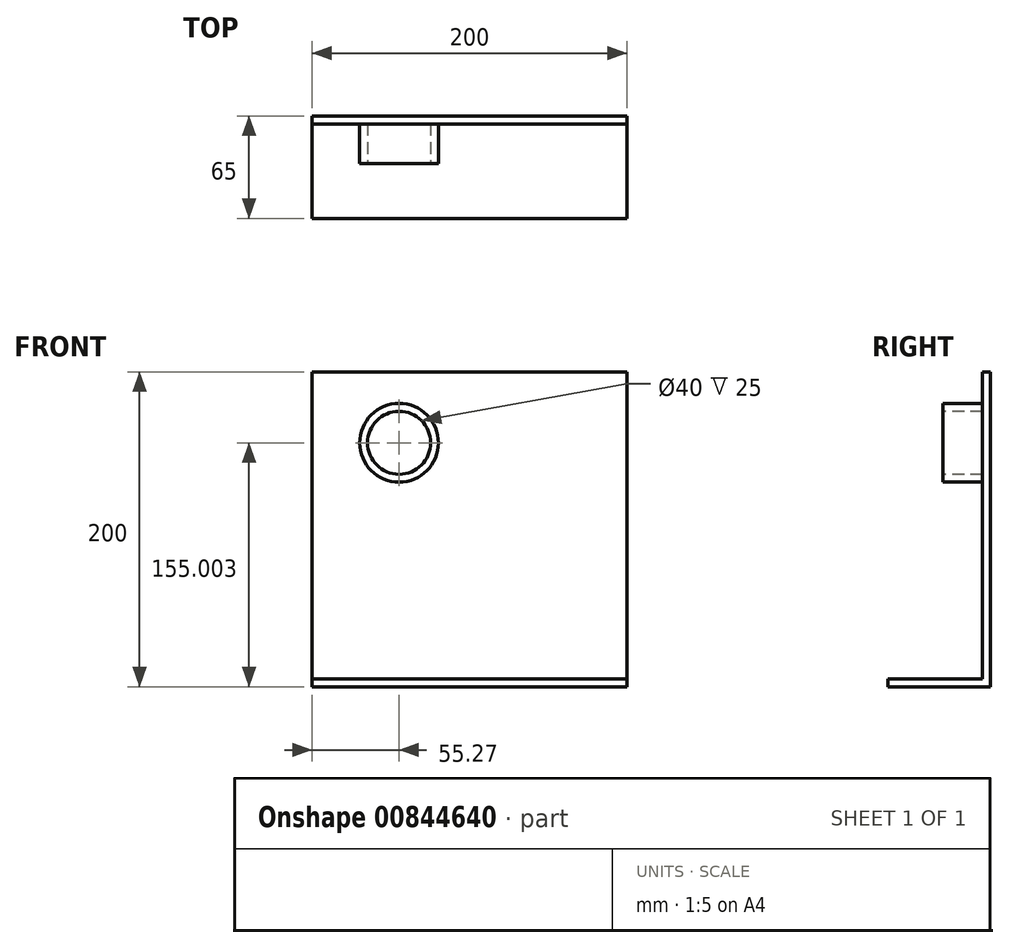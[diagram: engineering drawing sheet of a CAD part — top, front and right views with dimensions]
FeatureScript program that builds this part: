
annotation { "Feature Type Name" : "Feature", "Feature Type Description" : "" }
export const myFeature = defineFeature(function(context is Context, id is Id, definition is map)
    precondition{}
    {
        {
            var Q0;
            Q0=qCreatedBy(makeId("Front.planeOp"),FACE);
            var sketch = newSketch(context, id + "F0", { "sketchPlane" : qUnion([Q0])});
            skLineSegment(sketch, "E0.bottom", {"start": v(-55.27, -42.78) * mm, "end": v(144.73, -42.78) * mm});
            skLineSegment(sketch, "E0.top", {"start": v(-55.27, 157.22) * mm, "end": v(144.73, 157.22) * mm});
            skLineSegment(sketch, "E0.left", {"start": v(-55.27, -42.78) * mm, "end": v(-55.27, 157.22) * mm});
            skLineSegment(sketch, "E0.right", {"start": v(144.73, -42.78) * mm, "end": v(144.73, 157.22) * mm});
            skSolve(sketch);
        }
        {
            var Q0;
            Q0 = qSketchRegion(id + "F0", true);
            extrude(context, id + "F1", {"entities" : qUnion([Q0]), "depth" : 5 * mm, "offsetDistance" : 25 * mm});
        }
        {
            var Q0;
            Q0=makeQuery(id+"F1.opExtrude","CAP_FACE",FACE,{"disambiguationData":[OSD([sQuery(id+"F0.wireOp",EDGE,"E0.bottom"),sQuery(id+"F0.wireOp",EDGE,"E0.top"),sQuery(id+"F0.wireOp",EDGE,"E0.left"),sQuery(id+"F0.wireOp",EDGE,"E0.right")])],"isStart":false});
            var sketch = newSketch(context, id + "F2", { "sketchPlane" : qUnion([Q0])});
            skLineSegment(sketch, "E1.bottom", {"start": v(-55.27, -42.78) * mm, "end": v(144.73, -42.78) * mm});
            skLineSegment(sketch, "E1.top", {"start": v(-55.27, -37.78) * mm, "end": v(144.73, -37.78) * mm});
            skLineSegment(sketch, "E1.left", {"start": v(-55.27, -42.78) * mm, "end": v(-55.27, -37.78) * mm});
            skLineSegment(sketch, "E1.right", {"start": v(144.73, -42.78) * mm, "end": v(144.73, -37.78) * mm});
            skSolve(sketch);
        }
        {
            var Q0;
            Q0=makeQuery(id+"F2.imprint","IMPRINT",FACE,{"disambiguationData":[TD([[makeQuery(id+"F2.imprint","IMPRINT",EDGE,{"derivedFrom":sQuery(id+"F2.wireOp",EDGE,"E1.bottom")}),1.0]])]});
            extrude(context, id + "F3", {"entities" : qUnion([Q0]), "operationType" : NewBodyOperationType.ADD, "depth" : 60 * mm, "offsetDistance" : 25 * mm});
        }
        {
            var Q0;
            Q0=makeQuery(id+"F1.opExtrude","CAP_FACE",FACE,{"disambiguationData":[OSD([sQuery(id+"F0.wireOp",EDGE,"E0.bottom"),sQuery(id+"F0.wireOp",EDGE,"E0.top"),sQuery(id+"F0.wireOp",EDGE,"E0.left"),sQuery(id+"F0.wireOp",EDGE,"E0.right")])],"isStart":false});
            var sketch = newSketch(context, id + "F4", { "sketchPlane" : qUnion([Q0])});
            skCircle(sketch, "E2", {"center": v(0, 112.22) * mm, "radius": 25 * mm});
            skSolve(sketch);
        }
        {
            var Q0;
            Q0 = qSketchRegion(id + "F4", true);
            extrude(context, id + "F5", {"entities" : qUnion([Q0]), "operationType" : NewBodyOperationType.ADD, "depth" : 25 * mm, "offsetDistance" : 25 * mm});
        }
        {
            var Q0;
            Q0=makeQuery(id+"F5.opExtrude","CAP_FACE",FACE,{"disambiguationData":[OSD([sQuery(id+"F4.wireOp",EDGE,"E2")])],"isStart":false});
            var sketch = newSketch(context, id + "F6", { "sketchPlane" : qUnion([Q0])});
            skCircle(sketch, "E3", {"center": v(0, 112.22) * mm, "radius": 20 * mm});
            skSolve(sketch);
        }
        {
            var Q0;
            Q0 = qSketchRegion(id + "F6", true);
            extrude(context, id + "F7", {"entities" : qUnion([Q0]), "operationType" : NewBodyOperationType.REMOVE, "oppositeDirection" : true, "depth" : 25 * mm, "offsetDistance" : 25 * mm});
        }
    });
